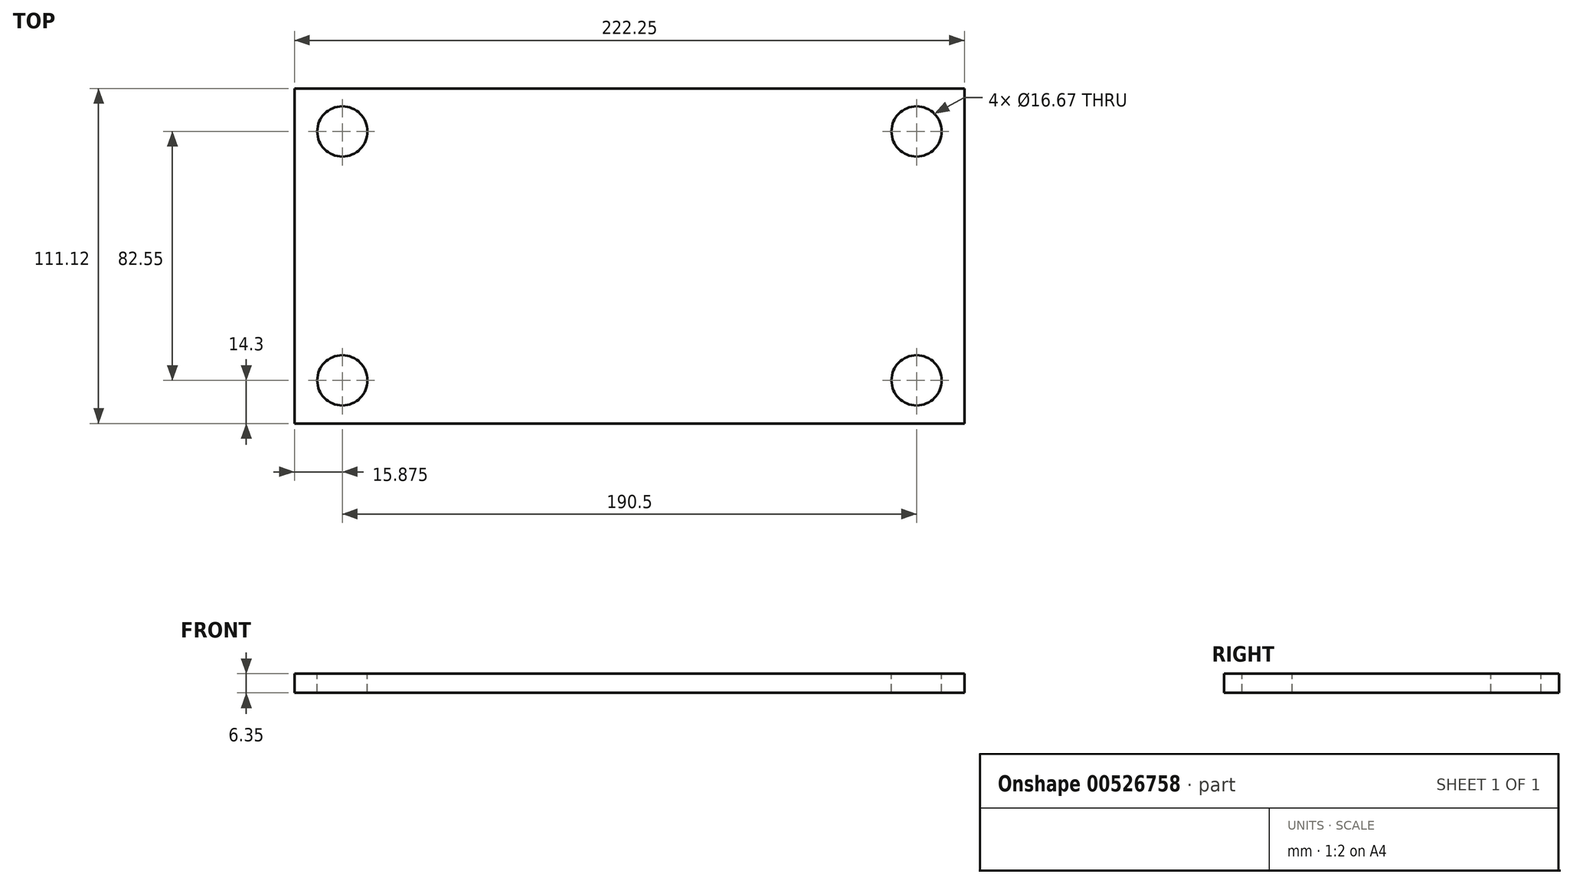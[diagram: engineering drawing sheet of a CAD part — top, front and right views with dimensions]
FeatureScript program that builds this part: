
annotation { "Feature Type Name" : "Feature", "Feature Type Description" : "" }
export const myFeature = defineFeature(function(context is Context, id is Id, definition is map)
    precondition{}
    {
        {
            var Q0;
            Q0=qCreatedBy(makeId("Top.planeOp"),FACE);
            var sketch = newSketch(context, id + "F0", { "sketchPlane" : qUnion([Q0])});
            skLineSegment(sketch, "E0.bottom", {"start": v(0, 0) * mm, "end": v(-222.25, 0) * mm});
            skLineSegment(sketch, "E0.top", {"start": v(0, 111.12) * mm, "end": v(-222.25, 111.12) * mm});
            skLineSegment(sketch, "E0.left", {"start": v(0, 0) * mm, "end": v(0, 111.12) * mm});
            skLineSegment(sketch, "E0.right", {"start": v(-222.25, 0) * mm, "end": v(-222.25, 111.12) * mm});
            skSolve(sketch);
        }
        {
            var Q0;
            Q0=makeQuery(id+"F0.imprint","IMPRINT",FACE,{"disambiguationData":[TD([[makeQuery(id+"F0.imprint","IMPRINT",EDGE,{"derivedFrom":sQuery(id+"F0.wireOp",EDGE,"E0.bottom")}),-1.0]])]});
            extrude(context, id + "F1", {"entities" : qUnion([Q0]), "depth" : 6.35 * mm, "offsetDistance" : 25.4 * mm});
        }
        {
            var Q0;
            Q0=makeQuery(id+"F1.opExtrude","CAP_FACE",FACE,{"disambiguationData":[OSD([sQuery(id+"F0.wireOp",EDGE,"E0.bottom"),sQuery(id+"F0.wireOp",EDGE,"E0.top"),sQuery(id+"F0.wireOp",EDGE,"E0.left"),sQuery(id+"F0.wireOp",EDGE,"E0.right")])],"isStart":false});
            var sketch = newSketch(context, id + "F2", { "sketchPlane" : qUnion([Q0])});
            skPoint(sketch, "E1", {"position": v(-206.38, 96.85) * mm});
            skPoint(sketch, "E2", {"position": v(-206.38, 14.3) * mm});
            skPoint(sketch, "E3", {"position": v(-15.88, 96.85) * mm});
            skPoint(sketch, "E4", {"position": v(-15.88, 14.3) * mm});
            skSolve(sketch);
        }
        {
            var Q0;
            Q0=sQuery(id+"F2.wireOp",VERTEX,"E1");
            var Q1;
            Q1=sQuery(id+"F2.wireOp",VERTEX,"E3");
            var Q2;
            Q2=sQuery(id+"F2.wireOp",VERTEX,"E4");
            var Q3;
            Q3=sQuery(id+"F2.wireOp",VERTEX,"E2");
            var Q4;
            Q4=makeQuery(id+"F1.opExtrude","SWEPT_BODY",BODY,{"disambiguationData":[OSD([sQuery(id+"F0.wireOp",EDGE,"E0.bottom"),sQuery(id+"F0.wireOp",EDGE,"E0.top"),sQuery(id+"F0.wireOp",EDGE,"E0.left"),sQuery(id+"F0.wireOp",EDGE,"E0.right")])]});
            hole(context, id + "F3", {"style" : HoleStyle.SIMPLE, "endStyle" : HoleEndStyle.THROUGH, "standardTappedOrClearance" : lookupTablePath({ "standard" : "ANSI", "fit" : "Normal (ASME)", "size" : "5/8", "type" : "Clearance" }), "standardBlindInLast" : lookupTablePath({ "fit" : "Free", "standard" : "ANSI", "size" : "5/8", "type" : "Clearance" }), "holeDiameter" : 16.67 * mm, "isTappedThrough" : true, "tappedDepth" : 12.7 * mm, "tapClearance" : 1, "locations" : qUnion([Q0, Q1, Q2, Q3]), "scope" : qUnion([Q4])});
        }
    });
